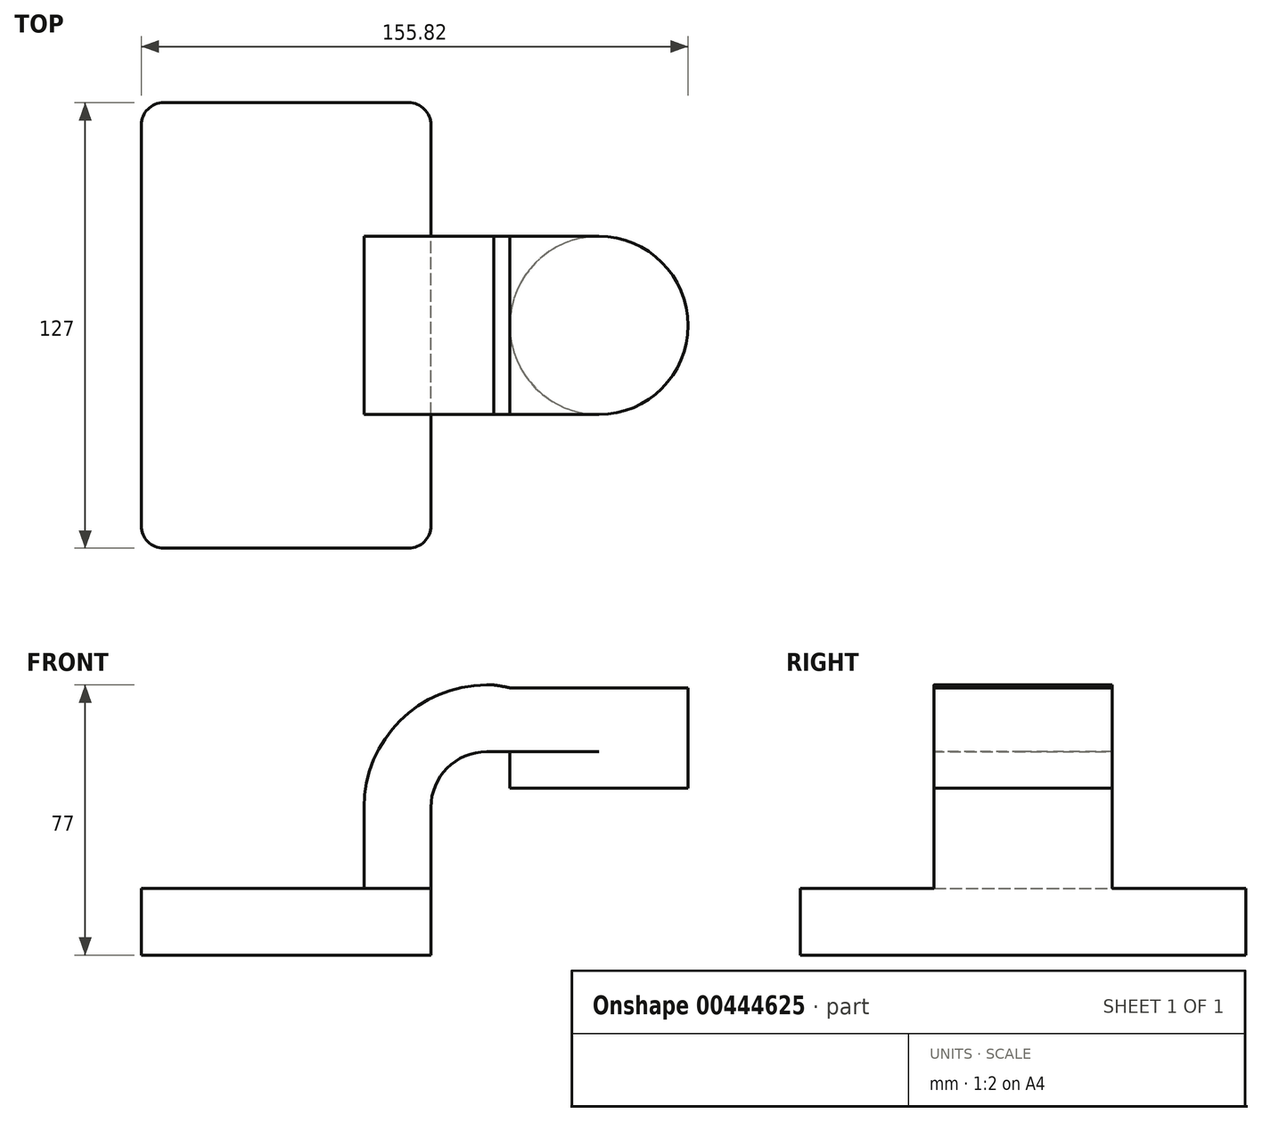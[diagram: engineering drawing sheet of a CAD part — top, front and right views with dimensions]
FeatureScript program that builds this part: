
annotation { "Feature Type Name" : "Feature", "Feature Type Description" : "" }
export const myFeature = defineFeature(function(context is Context, id is Id, definition is map)
    precondition{}
    {
        {
            var Q0;
            Q0=qCreatedBy(makeId("Front.planeOp"),FACE);
            var sketch = newSketch(context, id + "F0", { "sketchPlane" : qUnion([Q0])});
            skLineSegment(sketch, "E0.bottom", {"start": v(-41.27, -9.53) * mm, "end": v(41.28, -9.53) * mm});
            skLineSegment(sketch, "E0.top", {"start": v(-41.28, 9.53) * mm, "end": v(41.28, 9.53) * mm});
            skLineSegment(sketch, "E0.left", {"start": v(-41.28, -9.53) * mm, "end": v(-41.28, 9.53) * mm});
            skLineSegment(sketch, "E0.right", {"start": v(41.28, -9.53) * mm, "end": v(41.28, 9.53) * mm});
            skPoint(sketch, "E0.middle", {"position": v(0, 0) * mm});
            skLineSegment(sketch, "E1.bottom", {"start": v(63.75, 66.67) * mm, "end": v(114.55, 66.67) * mm});
            skLineSegment(sketch, "E1.top", {"start": v(63.75, 38.1) * mm, "end": v(114.55, 38.1) * mm});
            skLineSegment(sketch, "E1.left", {"start": v(63.75, 66.67) * mm, "end": v(63.75, 38.1) * mm});
            skLineSegment(sketch, "E1.right", {"start": v(114.55, 66.67) * mm, "end": v(114.55, 38.1) * mm});
            skPoint(sketch, "E1.middle", {"position": v(89.15, 52.39) * mm});
            skLineSegment(sketch, "E2", {"start": v(41.28, 9.52) * mm, "end": v(41.28, 32.55) * mm});
            skArc(sketch, "E3", {"start": v(41.27, 32.55) * mm, "mid": v(45.92, 43.77) * mm, "end": v(57.15, 48.42) * mm});
            skLineSegment(sketch, "E4", {"start": v(57.15, 48.42) * mm, "end": v(94.04, 48.42) * mm});
            skLineSegment(sketch, "E5.0", {"start": v(57.15, 67.47) * mm, "end": v(94.04, 67.47) * mm});
            skArc(sketch, "E5.1", {"start": v(22.22, 32.55) * mm, "mid": v(32.45, 57.24) * mm, "end": v(57.15, 67.47) * mm});
            skLineSegment(sketch, "E5.2", {"start": v(22.22, 9.52) * mm, "end": v(22.22, 32.55) * mm});
            skLineSegment(sketch, "E6", {"start": v(89.15, 38.1) * mm, "end": v(89.15, 67.47) * mm});
            skLineSegment(sketch, "E7", {"start": v(89.15, 67.47) * mm, "end": v(94.04, 67.47) * mm});
            skFitSpline(sketch, "E8", {"points": [v(-41.27, 9.52) * mm, v(63.75, 66.67) * mm], "startDerivative": vector(34.63, 120.3) * mm, "endDerivative": vector(124.64, -25.63) * mm});
            skSolve(sketch);
        }
        {
            var Q0;
            Q0=makeQuery(id+"F0.imprint","IMPRINT",FACE,{"disambiguationData":[TD([[makeQuery(id+"F0.imprint","IMPRINT",EDGE,{"derivedFrom":sQuery(id+"F0.wireOp",EDGE,"E0.bottom")}),1.0]])]});
            extrude(context, id + "F1", {"entities" : qUnion([Q0]), "endBound" : BoundingType.SYMMETRIC, "depth" : 127 * mm});
        }
        {
            var Q0;
            {var subQ1=sQuery(id+"F0.wireOp",EDGE,"E2");Q0=makeQuery(id+"F0.imprint","IMPRINT",FACE,{"disambiguationData":[TD([[makeQuery(id+"F0.imprint","IMPRINT",EDGE,{"derivedFrom":subQ1}),1.0]])]});}
            var Q1;
            {var subQ0=sQuery(id+"F0.wireOp",EDGE,"E1.left");var subQ5=sQuery(id+"F0.wireOp",EDGE,"E4");var subQ6=makeQuery(id+"F0.imprint","INTERSECT",VERTEX,{"derivedFrom":[subQ0,subQ5]});Q1=makeQuery(id+"F0.imprint","IMPRINT",FACE,{"disambiguationData":[TD([[makeQuery(id+"F0.imprint","IMPRINT",EDGE,{"disambiguationData":[TD([[subQ6,-1.0]])],"derivedFrom":subQ5}),1.0]])]});}
            extrude(context, id + "F2", {"entities" : qUnion([Q0, Q1]), "operationType" : NewBodyOperationType.ADD, "endBound" : BoundingType.SYMMETRIC, "depth" : 50.8 * mm});
        }
        {
            var Q0;
            {var subQ1=sQuery(id+"F0.wireOp",EDGE,"E5.1");Q0=makeQuery(id+"F0.imprint","IMPRINT",FACE,{"disambiguationData":[TD([[makeQuery(id+"F0.imprint","IMPRINT",EDGE,{"derivedFrom":subQ1}),1.0]])]});}
            extrude(context, id + "F3", {"entities" : qUnion([Q0]), "operationType" : NewBodyOperationType.ADD, "endBound" : BoundingType.SYMMETRIC, "depth" : 15.88 * mm});
        }
        {
            var Q0;
            {var subQ4=sQuery(id+"F0.wireOp",EDGE,"E1.right");Q0=makeQuery(id+"F0.imprint","IMPRINT",FACE,{"disambiguationData":[TD([[makeQuery(id+"F0.imprint","IMPRINT",EDGE,{"derivedFrom":subQ4}),-1.0]])]});}
            var Q1;
            Q1=sQuery(id+"F0.wireOp",EDGE,"E6");
            revolve(context, id + "F4", {"operationType" : NewBodyOperationType.ADD, "entities" : qUnion([Q0]), "axis" : qUnion([Q1]), "revolveType" : RevolveType.FULL});
        }
        {
            var Q0;
            Q0=makeQuery(id+"F1.opExtrude","CAP_EDGE",EDGE,{"disambiguationData":[OSD([sQuery(id+"F0.wireOp",EDGE,"E0.right")])],"isStart":false});
            var Q1;
            Q1=makeQuery(id+"F1.opExtrude","CAP_EDGE",EDGE,{"disambiguationData":[OSD([sQuery(id+"F0.wireOp",EDGE,"E0.left")])],"isStart":false});
            var Q2;
            Q2=makeQuery(id+"F1.opExtrude","CAP_EDGE",EDGE,{"disambiguationData":[OSD([sQuery(id+"F0.wireOp",EDGE,"E0.right")])],"isStart":true});
            var Q3;
            Q3=makeQuery(id+"F1.opExtrude","CAP_EDGE",EDGE,{"disambiguationData":[OSD([sQuery(id+"F0.wireOp",EDGE,"E0.left")])],"isStart":true});
            fillet(context, id + "F5", {"entities" : qUnion([Q0, Q1, Q2, Q3]), "radius" : 6.35 * mm, "tangentPropagation" : true, "allowEdgeOverflow" : false});
        }
    });
